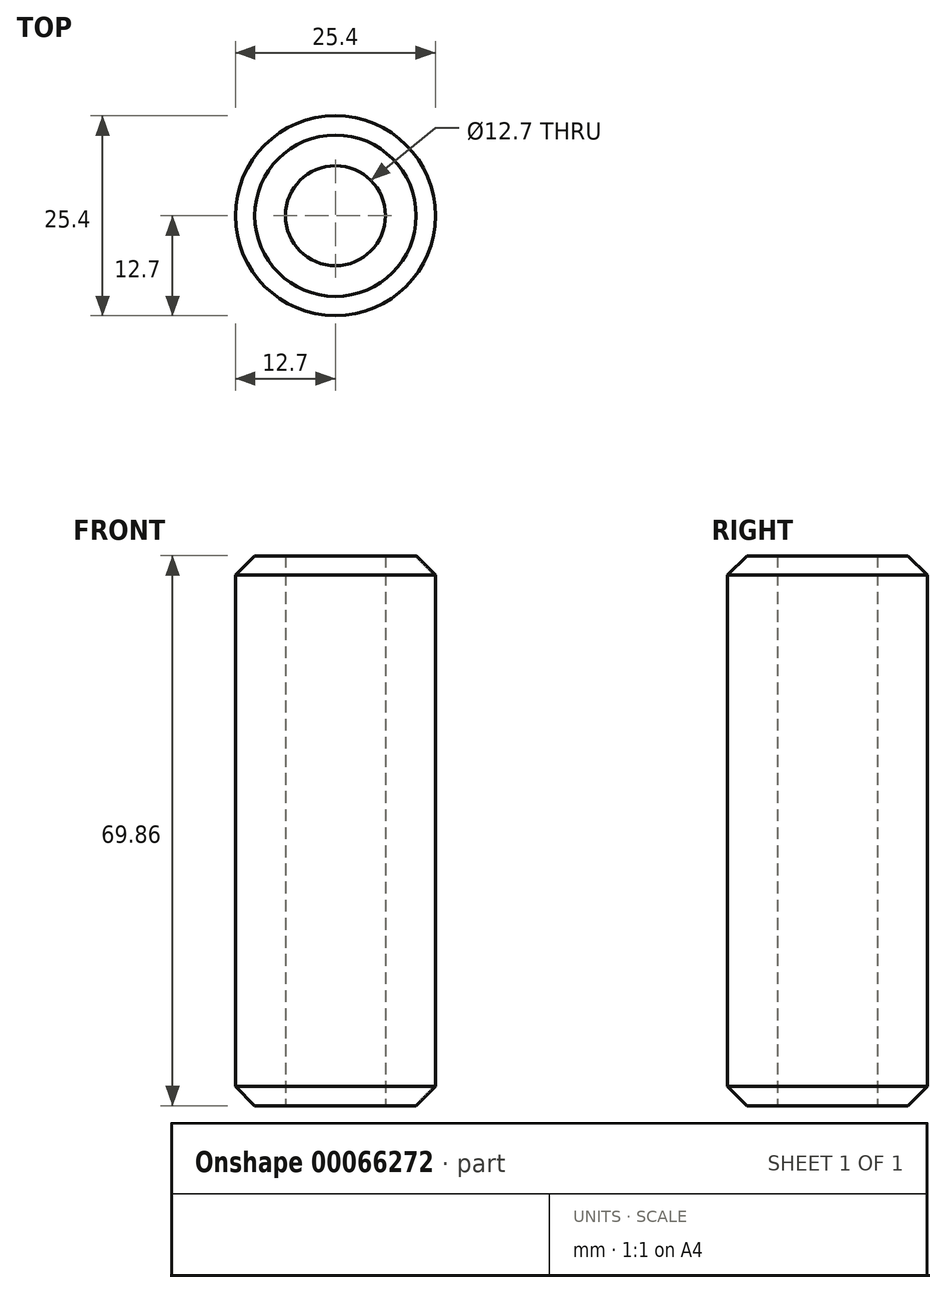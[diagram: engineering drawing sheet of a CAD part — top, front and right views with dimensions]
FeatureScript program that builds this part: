
annotation { "Feature Type Name" : "Feature", "Feature Type Description" : "" }
export const myFeature = defineFeature(function(context is Context, id is Id, definition is map)
    precondition{}
    {
        {
            var Q0;
            Q0=qCreatedBy(makeId("Top.planeOp"),FACE);
            var sketch = newSketch(context, id + "F0", { "sketchPlane" : qUnion([Q0])});
            skCircle(sketch, "E0", {"center": v(0, 0) * mm, "radius": 12.7 * mm});
            skCircle(sketch, "E1", {"center": v(0, 0) * mm, "radius": 6.35 * mm});
            skSolve(sketch);
        }
        {
            var Q0;
            Q0 = qSketchRegion(id + "F0", true);
            extrude(context, id + "F1", {"entities" : qUnion([Q0]), "endBound" : BoundingType.SYMMETRIC, "depth" : 69.85 * mm});
        }
        {
            var Q0;
            Q0=makeQuery(id+"F1.opExtrude","CAP_EDGE",EDGE,{"disambiguationData":[OSD([sQuery(id+"F0.wireOp",EDGE,"E0")])],"isStart":true});
            var Q1;
            Q1=makeQuery(id+"F1.opExtrude","CAP_EDGE",EDGE,{"disambiguationData":[OSD([sQuery(id+"F0.wireOp",EDGE,"E0")])],"isStart":false});
            chamfer(context, id + "F2", {"entities" : qUnion([Q0, Q1]), "width" : 2.45 * mm, "tangentPropagation" : true});
        }
    });
